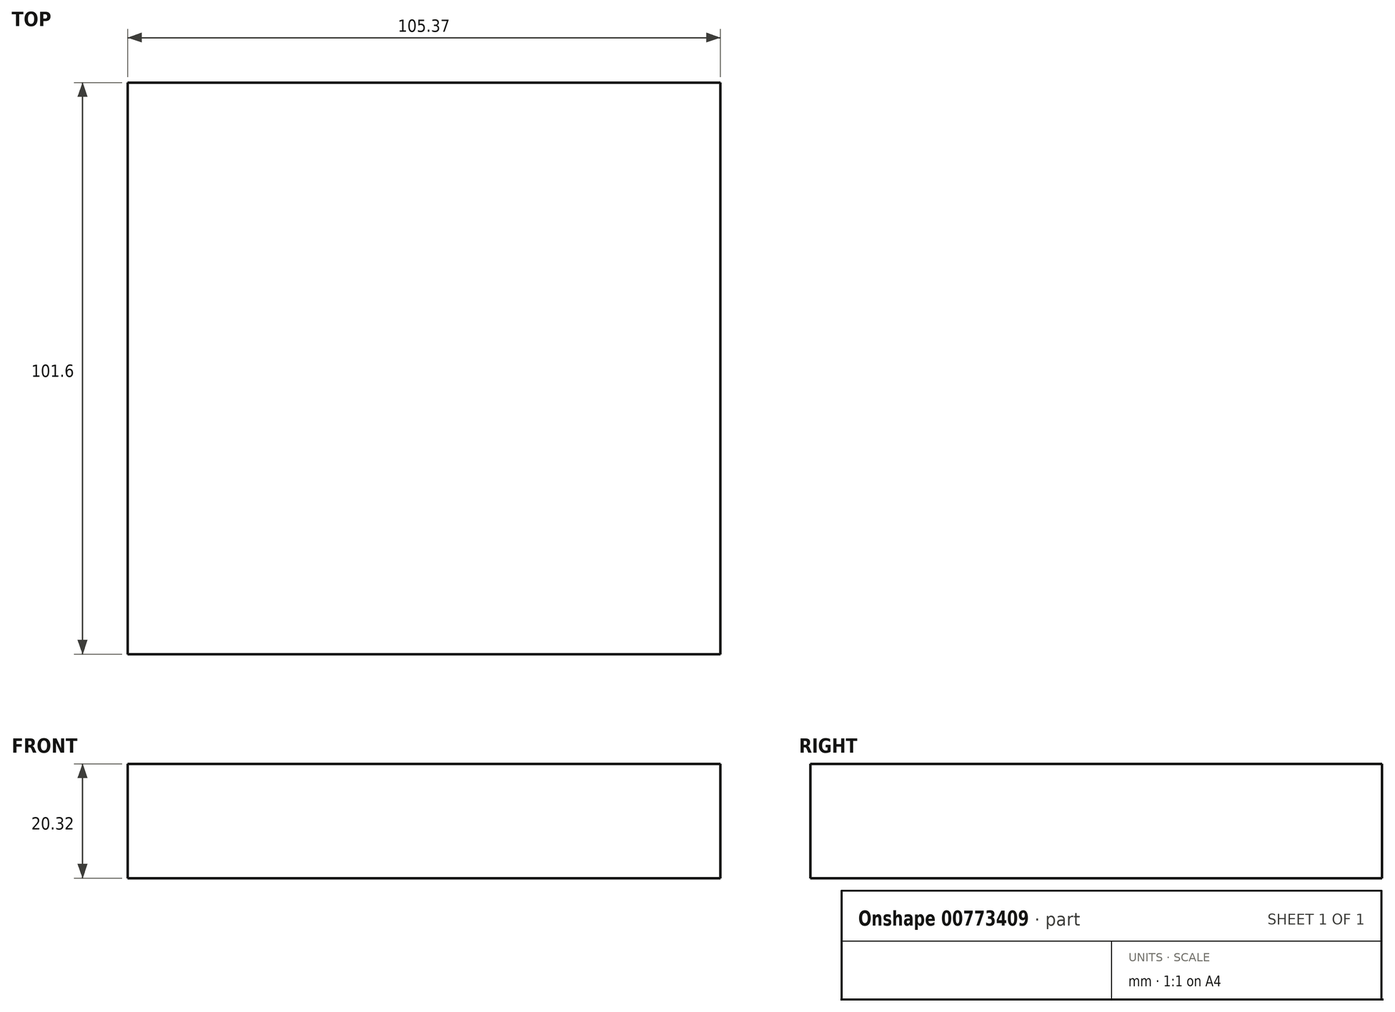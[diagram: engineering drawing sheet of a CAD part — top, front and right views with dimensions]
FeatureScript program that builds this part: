
annotation { "Feature Type Name" : "Feature", "Feature Type Description" : "" }
export const myFeature = defineFeature(function(context is Context, id is Id, definition is map)
    precondition{}
    {
        {
            var Q0;
            Q0=qCreatedBy(makeId("Front.planeOp"),FACE);
            var sketch = newSketch(context, id + "F0", { "sketchPlane" : qUnion([Q0])});
            skLineSegment(sketch, "E0", {"start": v(-53.34, 0) * mm, "end": v(-35.56, 0) * mm});
            skLineSegment(sketch, "E1", {"start": v(-35.56, 0) * mm, "end": v(-35.56, 30.82) * mm});
            skLineSegment(sketch, "E2", {"start": v(-35.56, 30.82) * mm, "end": v(0, 30.82) * mm});
            skLineSegment(sketch, "E3", {"start": v(0, 48.6) * mm, "end": v(-53.34, 48.6) * mm});
            skLineSegment(sketch, "E4", {"start": v(-53.34, 48.6) * mm, "end": v(-53.34, 0) * mm});
            skLineSegment(sketch, "E5.MirrorCS", {"start": v(0, 48.6) * mm, "end": v(47, 48.6) * mm});
            skLineSegment(sketch, "E6.MirrorCS", {"start": v(54.61, 40.98) * mm, "end": v(54.61, -1.27) * mm});
            skLineSegment(sketch, "E7.MirrorCS", {"start": v(53.34, 0) * mm, "end": v(35.56, 0) * mm});
            skLineSegment(sketch, "E8.MirrorCS", {"start": v(35.56, 30.82) * mm, "end": v(0, 30.82) * mm});
            skLineSegment(sketch, "E9.MirrorCS", {"start": v(35.56, 0) * mm, "end": v(35.56, 30.82) * mm});
            skPoint(sketch, "E10.visualSharp", {"position": v(54.61, 48.6) * mm});
            skArc(sketch, "E10.filletArc", {"start": v(54.61, 40.98) * mm, "mid": v(52.38, 46.36) * mm, "end": v(47, 48.6) * mm});
            skSolve(sketch);
        }
        {
            var Q0;
            Q0=sQuery(id+"F0.wireOp",EDGE,"E5.MirrorCS");
            var Q1;
            Q1=sQuery(id+"F0.wireOp",EDGE,"E10.filletArc");
            var Q2;
            Q2=sQuery(id+"F0.wireOp",EDGE,"E6.MirrorCS");
            var Q3;
            Q3=sQuery(id+"F0.wireOp",EDGE,"E7.MirrorCS");
            var Q4;
            Q4=sQuery(id+"F0.wireOp",EDGE,"E9.MirrorCS");
            var Q5;
            Q5=sQuery(id+"F0.wireOp",EDGE,"E8.MirrorCS");
            var Q6;
            Q6=sQuery(id+"F0.wireOp",EDGE,"E3");
            var Q7;
            Q7=sQuery(id+"F0.wireOp",EDGE,"E2");
            var Q8;
            Q8=sQuery(id+"F0.wireOp",EDGE,"E4");
            var Q9;
            Q9=sQuery(id+"F0.wireOp",EDGE,"E1");
            var Q10;
            Q10=sQuery(id+"F0.wireOp",EDGE,"E0");
            extrude(context, id + "F1", {"bodyType" : ToolBodyType.SURFACE, "surfaceEntities" : qUnion([Q0, Q1, Q2, Q3, Q4, Q5, Q6, Q7, Q8, Q9, Q10]), "depth" : 76.2 * mm, "offsetDistance" : 25.4 * mm});
        }
        {
            var Q0;
            Q0=qCreatedBy(makeId("Front.planeOp"),FACE);
            var sketch = newSketch(context, id + "F2", { "sketchPlane" : qUnion([Q0])});
            skLineSegment(sketch, "E11.bottom", {"start": v(-47.47, -55.15) * mm, "end": v(57.9, -55.15) * mm});
            skLineSegment(sketch, "E11.top", {"start": v(-47.47, -34.83) * mm, "end": v(57.9, -34.83) * mm});
            skLineSegment(sketch, "E11.left", {"start": v(-47.47, -55.15) * mm, "end": v(-47.47, -34.83) * mm});
            skLineSegment(sketch, "E11.right", {"start": v(57.9, -55.15) * mm, "end": v(57.9, -34.83) * mm});
            skSolve(sketch);
        }
        {
            var Q0;
            Q0 = qSketchRegion(id + "F2", true);
            extrude(context, id + "F3", {"entities" : qUnion([Q0]), "depth" : 101.6 * mm, "offsetDistance" : 25.4 * mm});
        }
    });
